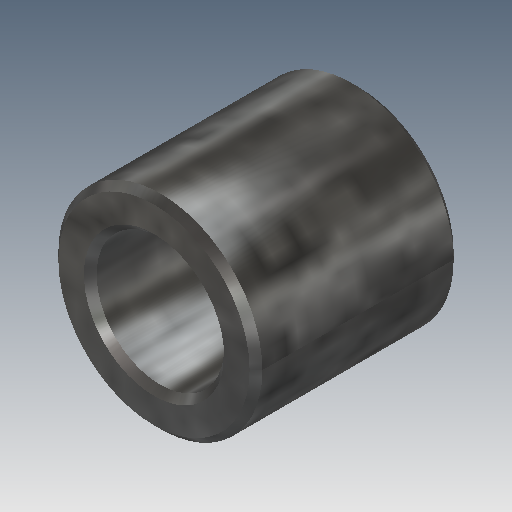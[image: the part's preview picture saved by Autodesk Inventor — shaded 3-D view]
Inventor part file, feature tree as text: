
AUTODESK INVENTOR PART (.ipt)
format: ipt  version: 2018 (Build 220112000, 112)  size: 191,488 bytes
history: native  units: mm
features: extrude x1, chamfer x1, sketch x1
ambient origin geometry x8: Origin, YZ Plane, XZ Plane, XY Plane, X Axis, Y Axis, Z Axis, Center Point
bodies: Solid1 (feature_tree)
feature tree (3):
  extrude  "Extrusion1"  Depth=16.0mm
  chamfer  "Chamfer1"  Distance=16.0mm
  sketch  "Sketch1"  dims[d0=10.0mm d1=16.0mm d2=16.0mm d3=0.0mm d4=0.5mm d5=2.0mm d6=45.0deg]
